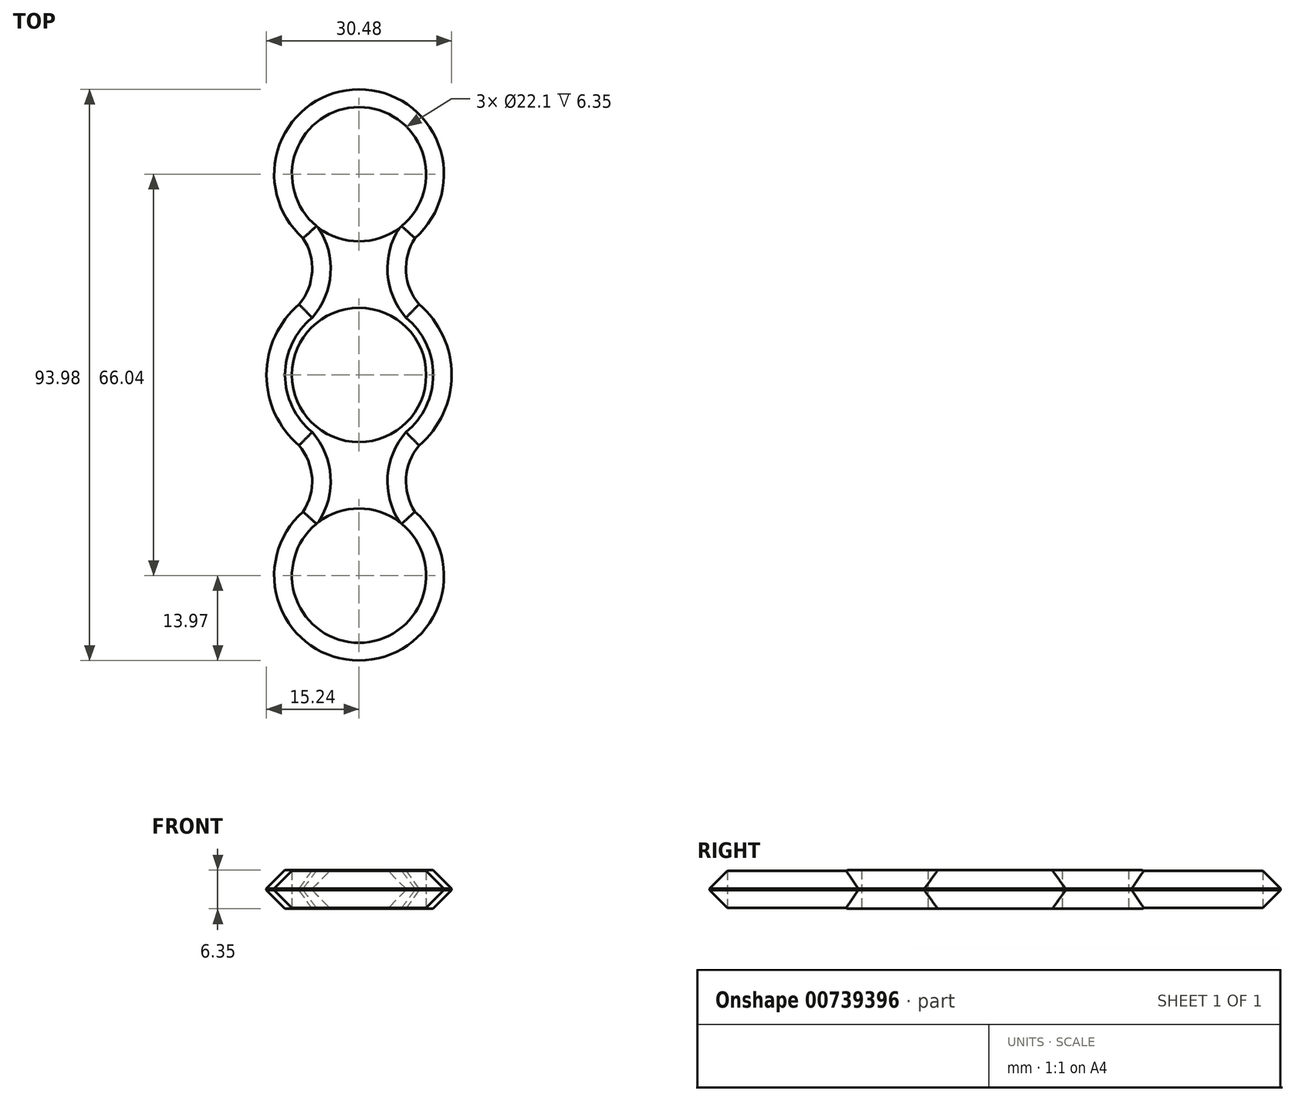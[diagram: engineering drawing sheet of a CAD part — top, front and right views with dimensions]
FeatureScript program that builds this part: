
annotation { "Feature Type Name" : "Feature", "Feature Type Description" : "" }
export const myFeature = defineFeature(function(context is Context, id is Id, definition is map)
    precondition{}
    {
        {
            var Q0;
            Q0=qCreatedBy(makeId("Top.planeOp"),FACE);
            var sketch = newSketch(context, id + "F0", { "sketchPlane" : qUnion([Q0])});
            skCircle(sketch, "E0", {"center": v(0, 0) * mm, "radius": 11.05 * mm});
            skCircle(sketch, "E1", {"center": v(0, 0) * mm, "radius": 15.24 * mm});
            skLineSegment(sketch, "E2", {"start": v(0, 19.05) * mm, "end": v(0, 21.97) * mm});
            skCircle(sketch, "E3", {"center": v(0, -33.02) * mm, "radius": 11.05 * mm});
            skCircle(sketch, "E4", {"center": v(0, 33.02) * mm, "radius": 11.05 * mm});
            skCircle(sketch, "E5", {"center": v(0, 33.02) * mm, "radius": 13.97 * mm});
            skCircle(sketch, "E6", {"center": v(0, -33.02) * mm, "radius": 13.97 * mm});
            skArc(sketch, "E7", {"start": v(-11.23, 10.3) * mm, "mid": v(-7.72, 17.51) * mm, "end": v(-11.24, 24.72) * mm});
            skArc(sketch, "E8", {"start": v(11.24, 24.72) * mm, "mid": v(7.72, 17.51) * mm, "end": v(11.23, 10.3) * mm});
            skArc(sketch, "E9", {"start": v(-11.23, -24.7) * mm, "mid": v(-7.72, -17.5) * mm, "end": v(-11.23, -10.3) * mm});
            skPoint(sketch, "E10.end.orphan", {"position": v(11.23, -10.3) * mm});
            skPoint(sketch, "E10.start.orphan", {"position": v(11.23, -24.7) * mm});
            skArc(sketch, "E11", {"start": v(11.23, -10.3) * mm, "mid": v(7.72, -17.5) * mm, "end": v(11.23, -24.7) * mm});
            skSolve(sketch);
        }
        {
            var Q0;
            Q0 = qSketchRegion(id + "F0", true);
            extrude(context, id + "F1", {"entities" : qUnion([Q0]), "depth" : 6.35 * mm, "offsetDistance" : 25.4 * mm});
        }
        {
            var Q0;
            Q0=makeQuery(id+"F1.opExtrude","CAP_EDGE",EDGE,{"disambiguationData":[OSD([sQuery(id+"F0.wireOp",EDGE,"E7")])],"isStart":false});
            var Q1;
            Q1=makeQuery(id+"F1.opExtrude","CAP_EDGE",EDGE,{"disambiguationData":[OSD([sQuery(id+"F0.wireOp",EDGE,"E5")])],"isStart":false});
            var Q2;
            Q2=makeQuery(id+"F1.opExtrude","CAP_EDGE",EDGE,{"disambiguationData":[OSD([sQuery(id+"F0.wireOp",EDGE,"E8")])],"isStart":false});
            var Q3;
            {var subQ0=sQuery(id+"F0.wireOp",EDGE,"E9");var subQ1=sQuery(id+"F0.wireOp",EDGE,"E1");var subQ2=makeQuery(id+"F0.imprint","INTERSECT",VERTEX,{"disambiguationData":[OD(0.0)],"derivedFrom":[subQ1,subQ0]});var subQ3=sQuery(id+"F0.wireOp",EDGE,"E7");var subQ4=makeQuery(id+"F0.imprint","INTERSECT",VERTEX,{"disambiguationData":[OD(0.0)],"derivedFrom":[subQ1,subQ3]});Q3=makeQuery(id+"F1.opExtrude","CAP_EDGE",EDGE,{"disambiguationData":[OSD([subQ1]),TDD([makeQuery(id+"F0.imprint","IMPRINT",EDGE,{"disambiguationData":[TD([[subQ4,1.0]])],"derivedFrom":subQ1}),makeQuery(id+"F0.imprint","IMPRINT",EDGE,{"disambiguationData":[TD([[subQ4,-1.0]])],"derivedFrom":subQ1}),makeQuery(id+"F0.imprint","IMPRINT",EDGE,{"disambiguationData":[TD([[subQ2,-1.0]])],"derivedFrom":subQ1})])],"isStart":false});}
            var Q4;
            Q4=makeQuery(id+"F1.opExtrude","CAP_EDGE",EDGE,{"disambiguationData":[OSD([sQuery(id+"F0.wireOp",EDGE,"E9")])],"isStart":false});
            var Q5;
            Q5=makeQuery(id+"F1.opExtrude","CAP_EDGE",EDGE,{"disambiguationData":[OSD([sQuery(id+"F0.wireOp",EDGE,"E6")])],"isStart":false});
            var Q6;
            Q6=makeQuery(id+"F1.opExtrude","CAP_EDGE",EDGE,{"disambiguationData":[OSD([sQuery(id+"F0.wireOp",EDGE,"E11")])],"isStart":false});
            var Q7;
            {var subQ0=sQuery(id+"F0.wireOp",EDGE,"E8");var subQ1=sQuery(id+"F0.wireOp",EDGE,"E1");var subQ2=makeQuery(id+"F0.imprint","INTERSECT",VERTEX,{"disambiguationData":[OD(0.0)],"derivedFrom":[subQ1,subQ0]});var subQ3=sQuery(id+"F0.wireOp",EDGE,"E11");var subQ4=makeQuery(id+"F0.imprint","INTERSECT",VERTEX,{"disambiguationData":[OD(0.0)],"derivedFrom":[subQ1,subQ3]});Q7=makeQuery(id+"F1.opExtrude","CAP_EDGE",EDGE,{"disambiguationData":[OSD([subQ1]),TDD([makeQuery(id+"F0.imprint","IMPRINT",EDGE,{"disambiguationData":[TD([[subQ2,-1.0]])],"derivedFrom":subQ1}),makeQuery(id+"F0.imprint","IMPRINT",EDGE,{"disambiguationData":[TD([[subQ4,1.0]])],"derivedFrom":subQ1}),makeQuery(id+"F0.imprint","IMPRINT",EDGE,{"disambiguationData":[TD([[subQ2,1.0]])],"derivedFrom":subQ1})])],"isStart":false});}
            var Q8;
            Q8=makeQuery(id+"F1.opExtrude","CAP_EDGE",EDGE,{"disambiguationData":[OSD([sQuery(id+"F0.wireOp",EDGE,"E6")])],"isStart":true});
            var Q9;
            Q9=makeQuery(id+"F1.opExtrude","CAP_EDGE",EDGE,{"disambiguationData":[OSD([sQuery(id+"F0.wireOp",EDGE,"E11")])],"isStart":true});
            var Q10;
            Q10=makeQuery(id+"F1.opExtrude","CAP_EDGE",EDGE,{"disambiguationData":[OSD([sQuery(id+"F0.wireOp",EDGE,"E9")])],"isStart":true});
            var Q11;
            {var subQ0=sQuery(id+"F0.wireOp",EDGE,"E9");var subQ1=sQuery(id+"F0.wireOp",EDGE,"E1");var subQ2=makeQuery(id+"F0.imprint","INTERSECT",VERTEX,{"disambiguationData":[OD(0.0)],"derivedFrom":[subQ1,subQ0]});var subQ3=sQuery(id+"F0.wireOp",EDGE,"E7");var subQ4=makeQuery(id+"F0.imprint","INTERSECT",VERTEX,{"disambiguationData":[OD(0.0)],"derivedFrom":[subQ1,subQ3]});Q11=makeQuery(id+"F1.opExtrude","CAP_EDGE",EDGE,{"disambiguationData":[OSD([subQ1]),TDD([makeQuery(id+"F0.imprint","IMPRINT",EDGE,{"disambiguationData":[TD([[subQ4,1.0]])],"derivedFrom":subQ1}),makeQuery(id+"F0.imprint","IMPRINT",EDGE,{"disambiguationData":[TD([[subQ4,-1.0]])],"derivedFrom":subQ1}),makeQuery(id+"F0.imprint","IMPRINT",EDGE,{"disambiguationData":[TD([[subQ2,-1.0]])],"derivedFrom":subQ1})])],"isStart":true});}
            var Q12;
            Q12=makeQuery(id+"F1.opExtrude","CAP_EDGE",EDGE,{"disambiguationData":[OSD([sQuery(id+"F0.wireOp",EDGE,"E7")])],"isStart":true});
            var Q13;
            Q13=makeQuery(id+"F1.opExtrude","CAP_EDGE",EDGE,{"disambiguationData":[OSD([sQuery(id+"F0.wireOp",EDGE,"E5")])],"isStart":true});
            var Q14;
            Q14=makeQuery(id+"F1.opExtrude","CAP_EDGE",EDGE,{"disambiguationData":[OSD([sQuery(id+"F0.wireOp",EDGE,"E8")])],"isStart":true});
            var Q15;
            {var subQ0=sQuery(id+"F0.wireOp",EDGE,"E8");var subQ1=sQuery(id+"F0.wireOp",EDGE,"E1");var subQ2=makeQuery(id+"F0.imprint","INTERSECT",VERTEX,{"disambiguationData":[OD(0.0)],"derivedFrom":[subQ1,subQ0]});var subQ3=sQuery(id+"F0.wireOp",EDGE,"E11");var subQ4=makeQuery(id+"F0.imprint","INTERSECT",VERTEX,{"disambiguationData":[OD(0.0)],"derivedFrom":[subQ1,subQ3]});Q15=makeQuery(id+"F1.opExtrude","CAP_EDGE",EDGE,{"disambiguationData":[OSD([subQ1]),TDD([makeQuery(id+"F0.imprint","IMPRINT",EDGE,{"disambiguationData":[TD([[subQ2,-1.0]])],"derivedFrom":subQ1}),makeQuery(id+"F0.imprint","IMPRINT",EDGE,{"disambiguationData":[TD([[subQ4,1.0]])],"derivedFrom":subQ1}),makeQuery(id+"F0.imprint","IMPRINT",EDGE,{"disambiguationData":[TD([[subQ2,1.0]])],"derivedFrom":subQ1})])],"isStart":true});}
            chamfer(context, id + "F2", {"entities" : qUnion([Q0, Q1, Q2, Q3, Q4, Q5, Q6, Q7, Q8, Q9, Q10, Q11, Q12, Q13, Q14, Q15]), "width" : 3.05 * mm, "tangentPropagation" : true});
        }
    });
